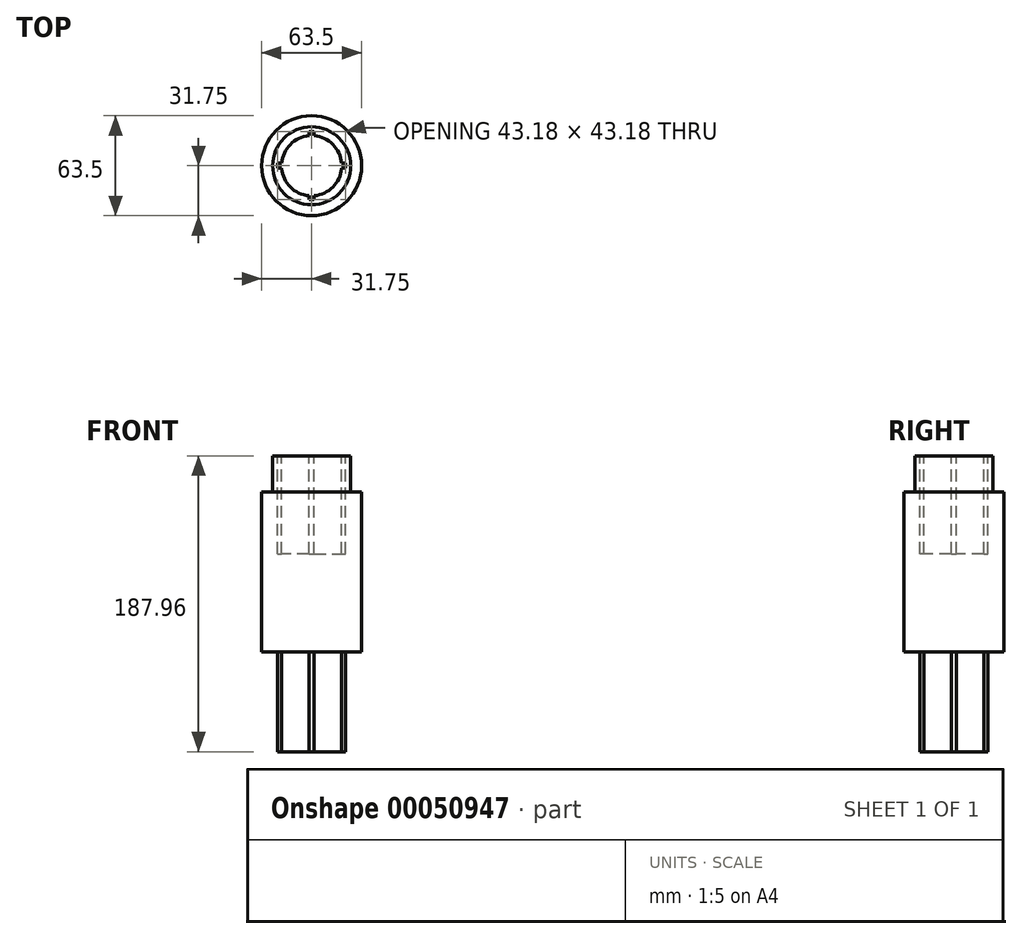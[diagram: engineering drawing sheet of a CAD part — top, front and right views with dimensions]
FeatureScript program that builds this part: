
annotation { "Feature Type Name" : "Feature", "Feature Type Description" : "" }
export const myFeature = defineFeature(function(context is Context, id is Id, definition is map)
    precondition{}
    {
        {
            var Q0;
            Q0=qCreatedBy(makeId("Top.planeOp"),FACE);
            var sketch = newSketch(context, id + "F0", { "sketchPlane" : qUnion([Q0])});
            skCircle(sketch, "E0", {"center": v(0, 0) * mm, "radius": 24.77 * mm});
            skSolve(sketch);
        }
        {
            var Q0;
            Q0=makeQuery(id+"F0.imprint","IMPRINT",FACE,{"disambiguationData":[TD([[makeQuery(id+"F0.imprint","IMPRINT",EDGE,{"derivedFrom":sQuery(id+"F0.wireOp",EDGE,"E0")}),1.0]])]});
            extrude(context, id + "F1", {"entities" : qUnion([Q0]), "depth" : 22.86 * mm});
        }
        {
            var Q0;
            Q0=makeQuery(id+"F1.opExtrude","CAP_FACE",FACE,{"disambiguationData":[OSD([sQuery(id+"F0.wireOp",EDGE,"E0")])],"isStart":true});
            var sketch = newSketch(context, id + "F2", { "sketchPlane" : qUnion([Q0])});
            skCircle(sketch, "E1", {"center": v(0, 0) * mm, "radius": 31.75 * mm});
            skSolve(sketch);
        }
        {
            var Q0;
            Q0=makeQuery(id+"F2.imprint","IMPRINT",FACE,{"disambiguationData":[TD([[makeQuery(id+"F2.imprint","IMPRINT",EDGE,{"derivedFrom":sQuery(id+"F2.wireOp",EDGE,"E1")}),1.0]])]});
            var Q1;
            Q1=makeQuery(id+"F2.imprint","IMPRINT",FACE,{"disambiguationData":[TD([[makeQuery(id+"F2.imprint","IMPRINT",EDGE,{"derivedFrom":makeQuery(id+"F1.opExtrude","CAP_EDGE",EDGE,{"disambiguationData":[OSD([sQuery(id+"F0.wireOp",EDGE,"E0")])],"isStart":true})}),-1.0]])]});
            extrude(context, id + "F3", {"entities" : qUnion([Q0, Q1]), "operationType" : NewBodyOperationType.ADD, "depth" : 101.6 * mm});
        }
        {
            var Q0;
            Q0=makeQuery(id+"F3.opExtrude","CAP_FACE",FACE,{"disambiguationData":[OSD([sQuery(id+"F2.wireOp",EDGE,"E1")])],"isStart":false});
            var sketch = newSketch(context, id + "F4", { "sketchPlane" : qUnion([Q0])});
            skLineSegment(sketch, "E2", {"start": v(-21.59, 0) * mm, "end": v(-21.59, 1.59) * mm});
            skLineSegment(sketch, "E3", {"start": v(-21.59, 1.59) * mm, "end": v(-19.05, 1.59) * mm});
            skLineSegment(sketch, "E4", {"start": v(-1.59, 19.05) * mm, "end": v(-1.59, 21.59) * mm});
            skLineSegment(sketch, "E5", {"start": v(-1.59, 21.59) * mm, "end": v(1.59, 21.59) * mm});
            skLineSegment(sketch, "E6", {"start": v(1.59, 21.59) * mm, "end": v(1.59, 19.05) * mm});
            skLineSegment(sketch, "E7", {"start": v(19.05, 1.59) * mm, "end": v(21.6, 1.59) * mm});
            skLineSegment(sketch, "E8", {"start": v(21.6, 1.59) * mm, "end": v(21.6, 0) * mm});
            skArc(sketch, "E9", {"start": v(19.05, 1.59) * mm, "mid": v(13.52, 13.52) * mm, "end": v(1.59, 19.05) * mm});
            skArc(sketch, "E10.trimOffspring", {"start": v(-1.59, 19.05) * mm, "mid": v(-13.52, 13.52) * mm, "end": v(-19.05, 1.59) * mm});
            skArc(sketch, "E11.MirrorCS", {"start": v(-1.59, -19.05) * mm, "mid": v(-13.52, -13.52) * mm, "end": v(-19.05, -1.59) * mm});
            skLineSegment(sketch, "E12.MirrorCS", {"start": v(-21.59, -1.59) * mm, "end": v(-19.05, -1.59) * mm});
            skLineSegment(sketch, "E13.MirrorCS", {"start": v(-21.59, 0) * mm, "end": v(-21.59, -1.59) * mm});
            skLineSegment(sketch, "E14.MirrorCS", {"start": v(-1.59, -19.05) * mm, "end": v(-1.59, -21.59) * mm});
            skLineSegment(sketch, "E15.MirrorCS", {"start": v(-1.59, -21.59) * mm, "end": v(1.59, -21.59) * mm});
            skLineSegment(sketch, "E16.MirrorCS", {"start": v(1.59, -21.59) * mm, "end": v(1.59, -19.05) * mm});
            skArc(sketch, "E17.MirrorCS", {"start": v(19.05, -1.59) * mm, "mid": v(13.52, -13.52) * mm, "end": v(1.59, -19.05) * mm});
            skLineSegment(sketch, "E18.MirrorCS", {"start": v(19.05, -1.59) * mm, "end": v(21.6, -1.59) * mm});
            skLineSegment(sketch, "E19.MirrorCS", {"start": v(21.6, -1.59) * mm, "end": v(21.6, 0) * mm});
            skSolve(sketch);
        }
        {
            var Q0;
            Q0=makeQuery(id+"F1.opExtrude","CAP_FACE",FACE,{"disambiguationData":[OSD([sQuery(id+"F0.wireOp",EDGE,"E0")])],"isStart":false});
            var sketch = newSketch(context, id + "F5", { "sketchPlane" : qUnion([Q0])});
            skLineSegment(sketch, "E20", {"start": v(-21.6, 0) * mm, "end": v(-21.6, 1.59) * mm});
            skLineSegment(sketch, "E21", {"start": v(-21.6, 1.59) * mm, "end": v(-19.05, 1.59) * mm});
            skLineSegment(sketch, "E22", {"start": v(-1.59, 19.05) * mm, "end": v(-1.59, 21.6) * mm});
            skLineSegment(sketch, "E23", {"start": v(-1.59, 21.6) * mm, "end": v(1.59, 21.6) * mm});
            skLineSegment(sketch, "E24", {"start": v(1.59, 21.6) * mm, "end": v(1.59, 19.05) * mm});
            skLineSegment(sketch, "E25", {"start": v(19.05, 1.59) * mm, "end": v(21.6, 1.59) * mm});
            skLineSegment(sketch, "E26", {"start": v(21.6, 1.59) * mm, "end": v(21.6, 0) * mm});
            skArc(sketch, "E27", {"start": v(19.05, 1.59) * mm, "mid": v(13.52, 13.52) * mm, "end": v(1.59, 19.05) * mm});
            skArc(sketch, "E28.trimOffspring", {"start": v(-1.59, 19.05) * mm, "mid": v(-13.52, 13.52) * mm, "end": v(-19.05, 1.59) * mm});
            skLineSegment(sketch, "E29.MirrorCS", {"start": v(-21.6, 0) * mm, "end": v(-21.6, -1.59) * mm});
            skLineSegment(sketch, "E30.MirrorCS", {"start": v(-21.6, -1.59) * mm, "end": v(-19.05, -1.59) * mm});
            skArc(sketch, "E31.MirrorCS", {"start": v(-1.59, -19.05) * mm, "mid": v(-13.52, -13.52) * mm, "end": v(-19.05, -1.59) * mm});
            skLineSegment(sketch, "E32.MirrorCS", {"start": v(-1.59, -19.05) * mm, "end": v(-1.59, -21.6) * mm});
            skLineSegment(sketch, "E33.MirrorCS", {"start": v(-1.59, -21.6) * mm, "end": v(1.59, -21.6) * mm});
            skArc(sketch, "E34.MirrorCS", {"start": v(19.05, -1.59) * mm, "mid": v(13.52, -13.52) * mm, "end": v(1.59, -19.05) * mm});
            skLineSegment(sketch, "E35.MirrorCS", {"start": v(19.05, -1.59) * mm, "end": v(21.6, -1.59) * mm});
            skLineSegment(sketch, "E36.MirrorCS", {"start": v(21.6, -1.59) * mm, "end": v(21.6, 0) * mm});
            skLineSegment(sketch, "E37.MirrorCS", {"start": v(1.59, -21.6) * mm, "end": v(1.59, -19.05) * mm});
            skSolve(sketch);
        }
        {
            var Q0;
            Q0=makeQuery(id+"F5.imprint","IMPRINT",FACE,{"disambiguationData":[TD([[makeQuery(id+"F5.imprint","IMPRINT",EDGE,{"derivedFrom":sQuery(id+"F5.wireOp",EDGE,"E20")}),-1.0]])]});
            var Q1;
            Q1=makeQuery(id+"F3.opExtrude","CAP_FACE",FACE,{"disambiguationData":[OSD([sQuery(id+"F2.wireOp",EDGE,"E1")])],"isStart":false});
            extrude(context, id + "F6", {"entities" : qUnion([Q0]), "operationType" : NewBodyOperationType.REMOVE, "oppositeDirection" : true, "endBoundEntityFace" : qUnion([Q1]), "depth" : 62.23 * mm});
        }
        {
            var Q0;
            Q0=makeQuery(id+"F4.imprint","IMPRINT",FACE,{"disambiguationData":[TD([[makeQuery(id+"F4.imprint","IMPRINT",EDGE,{"derivedFrom":sQuery(id+"F4.wireOp",EDGE,"E2")}),-1.0]])]});
            extrude(context, id + "F7", {"entities" : qUnion([Q0]), "operationType" : NewBodyOperationType.ADD, "depth" : 63.5 * mm});
        }
    });
